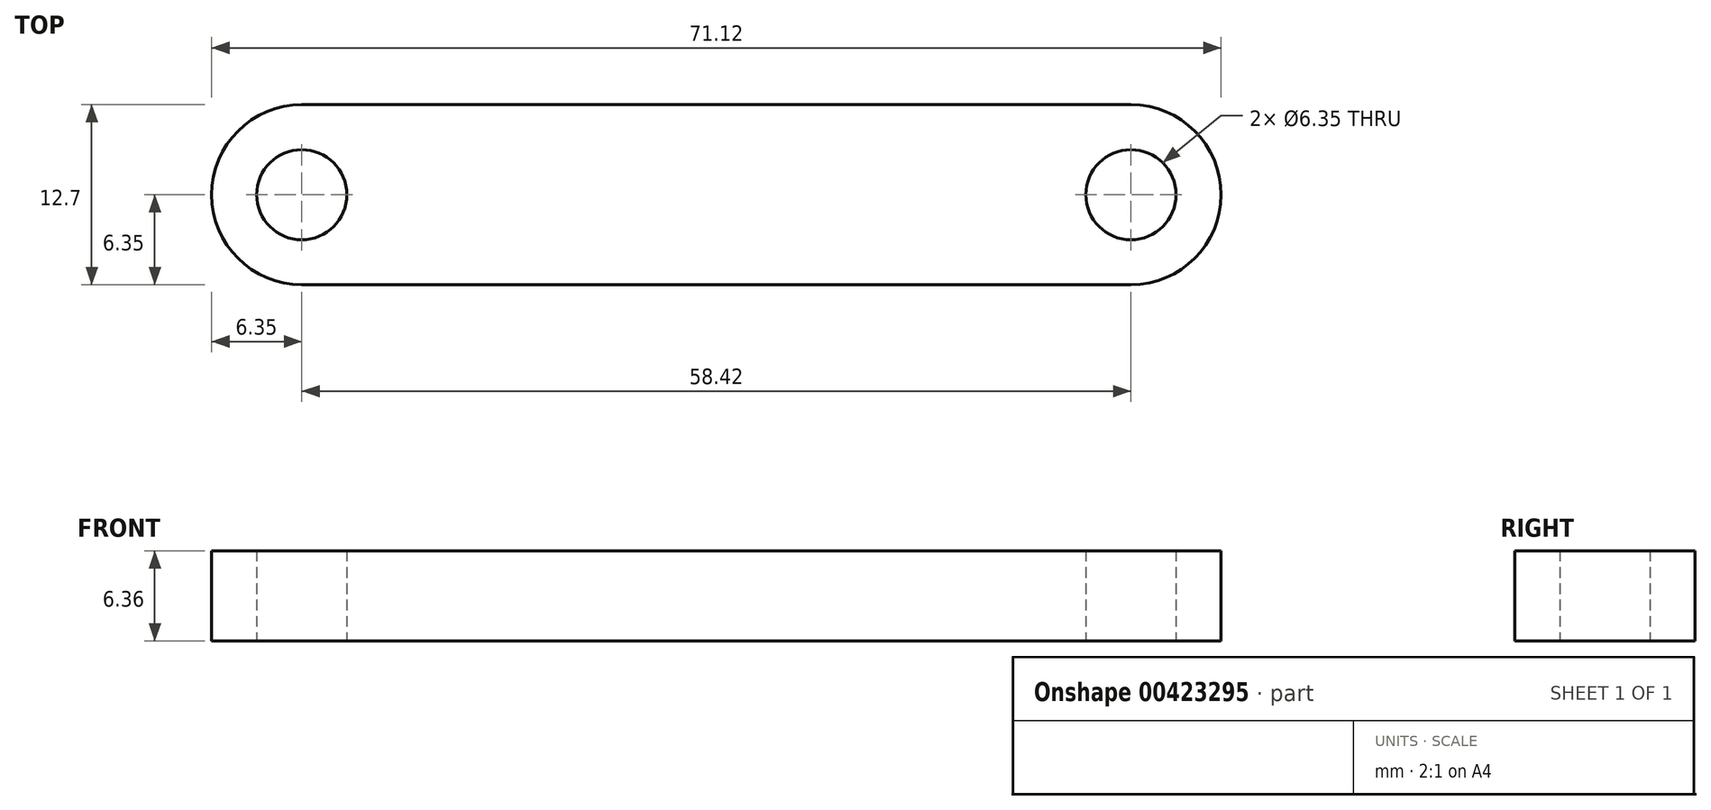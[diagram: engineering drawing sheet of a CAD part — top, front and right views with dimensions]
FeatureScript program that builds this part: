
annotation { "Feature Type Name" : "Feature", "Feature Type Description" : "" }
export const myFeature = defineFeature(function(context is Context, id is Id, definition is map)
    precondition{}
    {
        {
            var Q0;
            Q0=qCreatedBy(makeId("Top.planeOp"),FACE);
            var sketch = newSketch(context, id + "F0", { "sketchPlane" : qUnion([Q0])});
            skCircle(sketch, "E0", {"center": v(-29.21, 0) * mm, "radius": 3.18 * mm});
            skCircle(sketch, "E1", {"center": v(29.21, 0) * mm, "radius": 3.18 * mm});
            skArc(sketch, "E2", {"start": v(-29.21, 6.35) * mm, "mid": v(-35.56, 0) * mm, "end": v(-29.2, -6.35) * mm});
            skArc(sketch, "E3", {"start": v(29.21, -6.35) * mm, "mid": v(35.56, 0) * mm, "end": v(29.21, 6.35) * mm});
            skLineSegment(sketch, "E4", {"start": v(-29.2, 6.35) * mm, "end": v(29.21, 6.35) * mm});
            skLineSegment(sketch, "E5", {"start": v(29.21, -6.35) * mm, "end": v(-29.2, -6.35) * mm});
            skSolve(sketch);
        }
        {
            var Q0;
            Q0 = qSketchRegion(id + "F0", true);
            extrude(context, id + "F1", {"entities" : qUnion([Q0]), "endBound" : BoundingType.SYMMETRIC, "depth" : 6.35 * mm});
        }
    });
